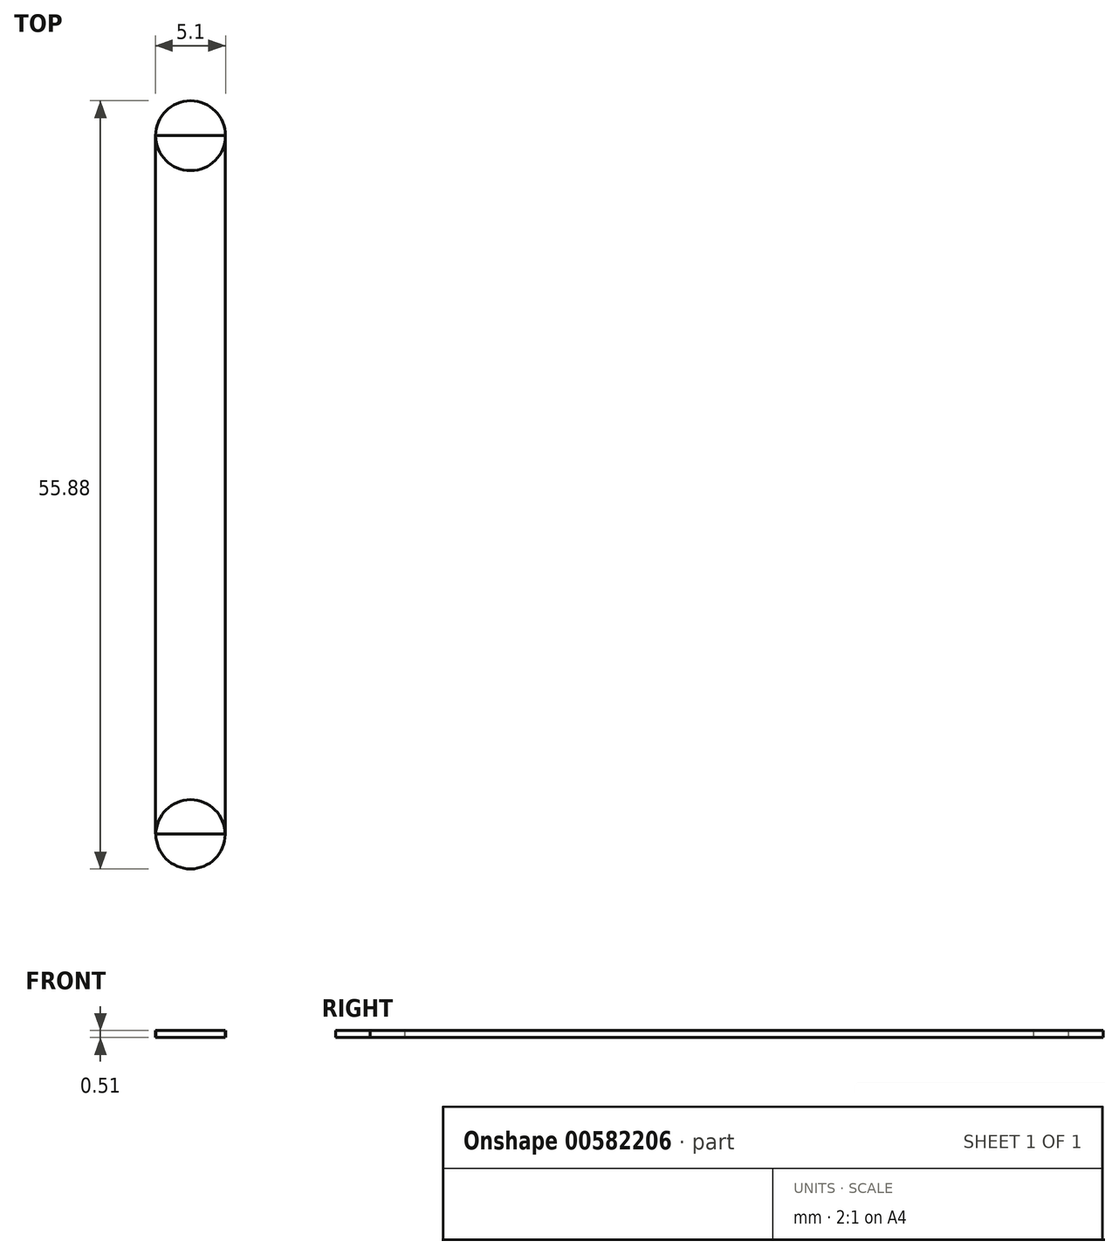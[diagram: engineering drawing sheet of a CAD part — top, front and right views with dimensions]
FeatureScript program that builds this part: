
annotation { "Feature Type Name" : "Feature", "Feature Type Description" : "" }
export const myFeature = defineFeature(function(context is Context, id is Id, definition is map)
    precondition{}
    {
        {
            var Q0;
            Q0=qCreatedBy(makeId("Top.planeOp"),FACE);
            var sketch = newSketch(context, id + "F0", { "sketchPlane" : qUnion([Q0])});
            skLineSegment(sketch, "E0.bottom", {"start": v(-56.95, 65.12) * mm, "end": v(-51.87, 65.12) * mm});
            skLineSegment(sketch, "E0.top", {"start": v(-56.95, 14.32) * mm, "end": v(-51.87, 14.32) * mm});
            skLineSegment(sketch, "E0.left", {"start": v(-56.95, 65.12) * mm, "end": v(-56.95, 14.32) * mm});
            skLineSegment(sketch, "E0.right", {"start": v(-51.87, 65.12) * mm, "end": v(-51.87, 14.32) * mm});
            skSolve(sketch);
        }
        {
            var Q0;
            Q0=qCreatedBy(makeId("Top.planeOp"),FACE);
            var sketch = newSketch(context, id + "F1", { "sketchPlane" : qUnion([Q0])});
            skCircle(sketch, "E1", {"center": v(-54.4, 65.13) * mm, "radius": 2.54 * mm});
            skCircle(sketch, "E2", {"center": v(-54.4, 14.31) * mm, "radius": 2.52 * mm});
            skSolve(sketch);
        }
        {
            var Q0;
            Q0=qCreatedBy(makeId("Top.planeOp"),FACE);
            var sketch = newSketch(context, id + "F2", { "sketchPlane" : qUnion([Q0])});
            skSolve(sketch);
        }
        {
            var Q0;
            Q0 = qSketchRegion(id + "F2", true);
            var Q1;
            Q1=makeQuery(id+"F0.imprint","IMPRINT",FACE,{"disambiguationData":[TD([[makeQuery(id+"F0.imprint","IMPRINT",EDGE,{"derivedFrom":sQuery(id+"F0.wireOp",EDGE,"E0.bottom")}),-1.0]])]});
            var Q2;
            Q2=makeQuery(id+"F1.imprint","IMPRINT",FACE,{"disambiguationData":[TD([[makeQuery(id+"F1.imprint","IMPRINT",EDGE,{"derivedFrom":sQuery(id+"F1.wireOp",EDGE,"E1")}),1.0]])]});
            var Q3;
            Q3=makeQuery(id+"F1.imprint","IMPRINT",FACE,{"disambiguationData":[TD([[makeQuery(id+"F1.imprint","IMPRINT",EDGE,{"derivedFrom":sQuery(id+"F1.wireOp",EDGE,"E2")}),1.0]])]});
            extrude(context, id + "F3", {"entities" : qUnion([Q0, Q1, Q2, Q3]), "depth" : 0.5 * mm, "offsetDistance" : 25.4 * mm});
        }
    });
